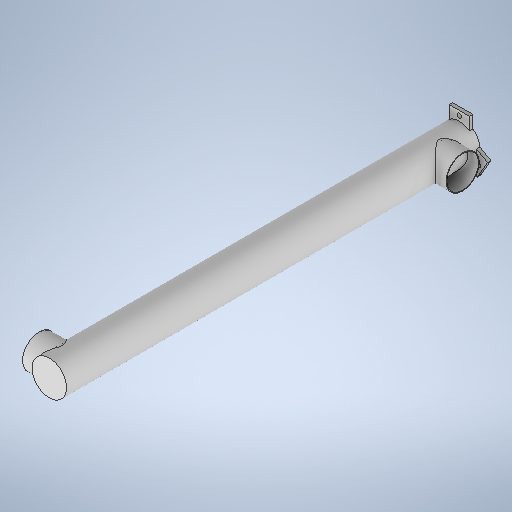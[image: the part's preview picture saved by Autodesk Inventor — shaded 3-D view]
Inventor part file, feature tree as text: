
AUTODESK INVENTOR PART (.ipt)
format: ipt  version: 2025 (Build 290162010, 162A)  size: 450,560 bytes
history: native  units: mm
features: extrude x6, sketch x4, projected_geometry x3, other x2, pattern_circular x1
ambient origin geometry x8: Origin, YZ Plane, XZ Plane, XY Plane, X Axis, Y Axis, Z Axis, Center Point
bodies: Solid1 (feature_tree)
feature tree (16):
  extrude  "Extrusion1"  Depth=70.0mm
  pattern_circular  "Circular Pattern1"  [2 undecoded]
  extrude  "Extrusion2"  Depth=1158.0mm TaperAngle=360.0deg
  extrude  "Extrusion3"  Depth=1158.0mm
  extrude  "Extrusion4"  Depth=1158.0mm TaperAngle=0.0deg
  extrude  "Extrusion5"  Depth=1158.0mm
  extrude  "Extrusion6"  Depth=83.0mm
  sketch  "Sketch1"  dims[d9=60.0mm d10=70.0mm]
  other  "Image1"
  sketch  "Sketch4"  dims[d15=13.0mm d16=10.0mm d17=0.0mm d18=30.0mm d19=360.0deg d21=101.6mm d22=1211.0mm d23=0.0mm d24=97.5mm d25=83.0mm d26=82.8mm d27=0.0mm d28=97.5mm d30=82.8mm d31=0.0mm d71=180.0mm d90=89.980359mm d93=53.0mm d94=220.0mm d95=180.0mm d96=16.0mm d97=80.0mm d99=360.0deg d101=20.0mm d102=0.0mm d103=2.0mm d105=80.0mm d106=220.0mm d107=180.0mm d108=16.0mm d109=360.0deg d110=20.0mm d111=0.0mm d112=2.0mm d114=1158.0mm]
  other  "Image2"
  projected_geometry  "Projected Loop1"
  projected_geometry  "Projected Loop2"
  sketch  "Sketch Circular Pattern1"  dims[d13=78.0mm]
  sketch  "Sketch Circular Pattern2"  dims[d14=13.0mm]
  projected_geometry  "Projected Loop3"
note: 2 required parameter values undecoded (feature->parameter linkage not recoverable at this tier; creation-order binding heuristic only, values carry confidence <= 0.55)
